# Revit family: AD-S4T - X Mount
name_source: partatom
category: Generic Models
revit_build: Autodesk Revit 2014 (Build: 20130308_1515(x64)
units: mm (PartAtom-declared; Revit-internal decimal feet)

## types (1)
- AD-S4T - X Mount
    100V Taps = 30, 15, 7.5
    70V Taps = 30, 15, 7.5, 3.75
    Coverage Horizontal = 120.00°
    Coverage Vertical = 120.00°
    Default Elevation = 4' - 0"
    Depth = 0' - 11 23/32"
    Description = 4" 2-Way Surface Mount Loudspeaker
    Height = 1' - 8 5/16"
    Impedance = 8
    Manufacturer = QSC Audio Products, LLC
    Manufacturer URL = www.qscaudio.com
    Model = AD-S4T
    Mount Depth = 0' - 0 31/32"
    Mount Height = 0' - 5 9/32"
    Mount Width = 0' - 4 11/32"
    Power Handling = 50
    Product Documentation Link = TBA
    Product Page URL = TBA
    Regulatory Compliance = RoHS
    SPL Max = 110
    Sensitivity = 87
    URL = TBA
    Weight Dimensional (kg) = 7.65
    Weight Dimensional (lb) = 16.8
    Weight Product (kg) = 2.9
    Weight Product (lb) = 6.5
    Width = 1' - 0 17/32"

## geometry (parser evidence)
native form markers: Blend x4, Sweep x32
no freeform markers — native parametric forms only
